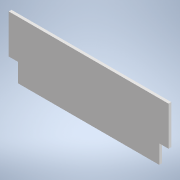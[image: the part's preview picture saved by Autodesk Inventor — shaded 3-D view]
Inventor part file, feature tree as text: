
AUTODESK INVENTOR PART (.ipt)
format: ipt  version: 2020 (Build 240168000, 168)  size: 92,160 bytes
history: native  units: mm
features: other x1, extrude x1, sketch x1
ambient origin geometry x8: Origin, YZ Plane, XZ Plane, XY Plane, X Axis, Y Axis, Z Axis, Center Point
bodies: Body1 (feature_tree)
feature tree (3):
  other  "Sólido1"
  extrude  "Extrusão1"  [1 undecoded]
  sketch  "Esboço1"  dims[d2=1.5mm d3=0.0mm]
note: 1 required parameter value undecoded (feature->parameter linkage not recoverable at this tier; creation-order binding heuristic only, values carry confidence <= 0.55)
